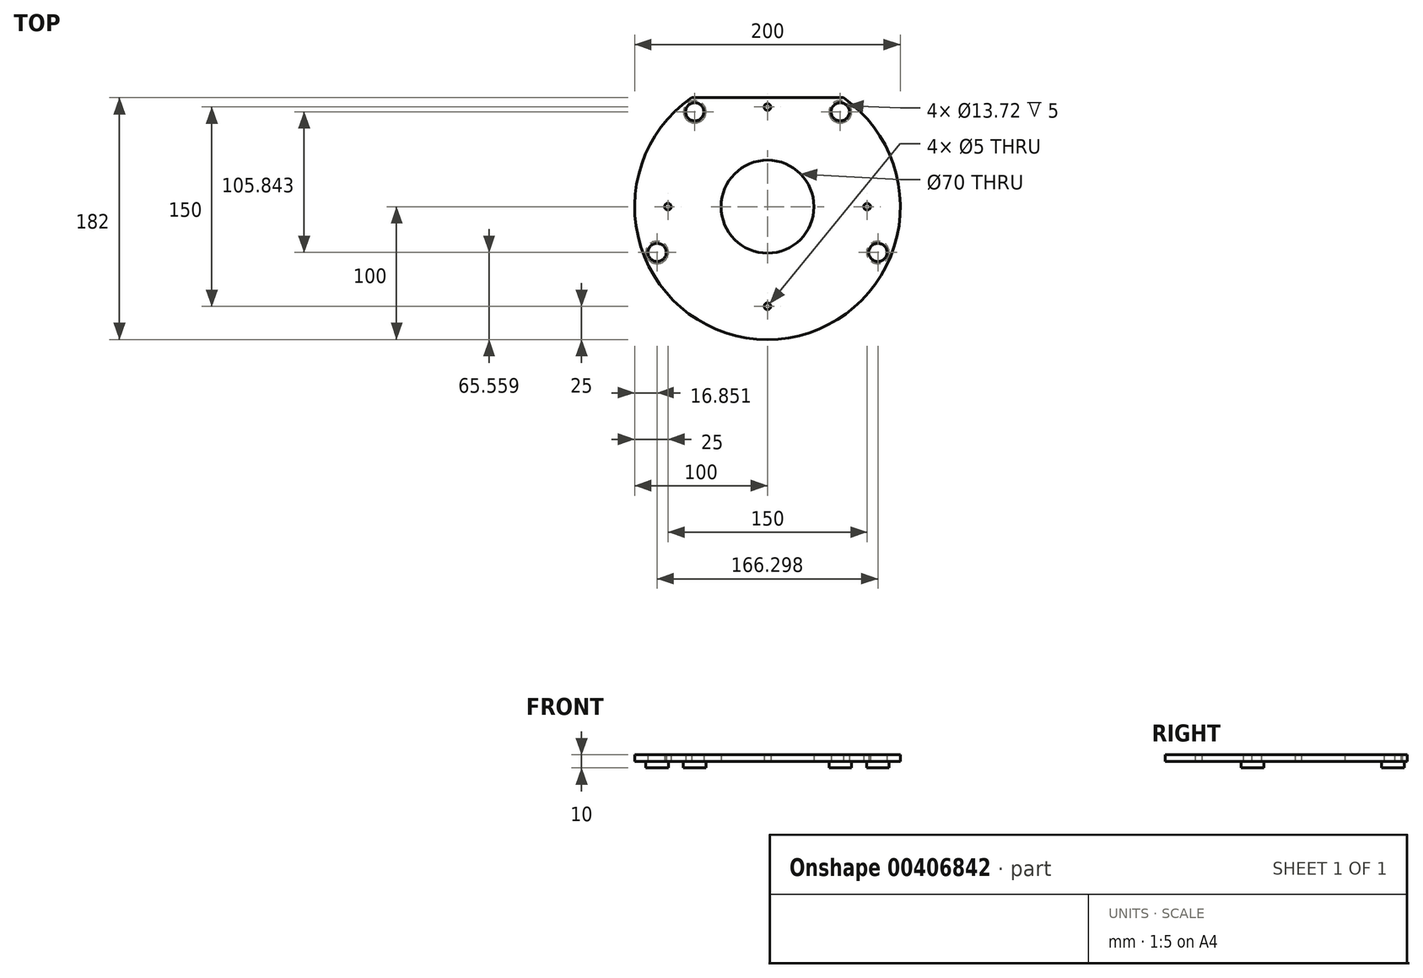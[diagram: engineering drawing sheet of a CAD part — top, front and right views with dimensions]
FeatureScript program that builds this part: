
annotation { "Feature Type Name" : "Feature", "Feature Type Description" : "" }
export const myFeature = defineFeature(function(context is Context, id is Id, definition is map)
    precondition{}
    {
        {
            var Q0;
            Q0=qCreatedBy(makeId("Top.planeOp"),FACE);
            var sketch = newSketch(context, id + "F0", { "sketchPlane" : qUnion([Q0])});
            skArc(sketch, "E0", {"start": v(-57.24, 82) * mm, "mid": v(0, -100) * mm, "end": v(57.24, 82) * mm});
            skCircle(sketch, "E1", {"center": v(-83.15, -34.44) * mm, "radius": 6.86 * mm});
            skLineSegment(sketch, "E2", {"start": v(-83.15, -34.44) * mm, "end": v(0, 0) * mm, "construction": true});
            skCircle(sketch, "E3.1.0", {"center": v(-54.79, 71.4) * mm, "radius": 6.86 * mm});
            skCircle(sketch, "E3.2.0", {"center": v(54.79, 71.4) * mm, "radius": 6.86 * mm});
            skCircle(sketch, "E3.3.0", {"center": v(83.15, -34.44) * mm, "radius": 6.86 * mm});
            skLineSegment(sketch, "E3.anchor1", {"start": v(0, 0) * mm, "end": v(-83.15, -34.44) * mm, "construction": true});
            skLineSegment(sketch, "E3.anchor2", {"start": v(0, 0) * mm, "end": v(83.15, -34.44) * mm, "construction": true});
            skLineSegment(sketch, "E4", {"start": v(-57.24, 82) * mm, "end": v(57.24, 82) * mm});
            skCircle(sketch, "E5", {"center": v(0, 0) * mm, "radius": 35 * mm});
            skCircle(sketch, "E6", {"center": v(-75, 0) * mm, "radius": 2.5 * mm});
            skCircle(sketch, "E7.1.0", {"center": v(0, -75) * mm, "radius": 2.5 * mm});
            skCircle(sketch, "E7.2.0", {"center": v(75, 0) * mm, "radius": 2.5 * mm});
            skCircle(sketch, "E7.3.0", {"center": v(0, 75) * mm, "radius": 2.5 * mm});
            skSolve(sketch);
        }
        {
            var Q0;
            Q0 = qSketchRegion(id + "F0", true);
            extrude(context, id + "F1", {"entities" : qUnion([Q0]), "depth" : 5 * mm});
        }
        {
            var Q0;
            Q0=makeQuery(id+"F1.opExtrude","CAP_FACE",FACE,{"disambiguationData":[OSD([sQuery(id+"F0.wireOp",EDGE,"E0"),sQuery(id+"F0.wireOp",EDGE,"E1"),sQuery(id+"F0.wireOp",EDGE,"E3.1.0"),sQuery(id+"F0.wireOp",EDGE,"E3.2.0"),sQuery(id+"F0.wireOp",EDGE,"E3.3.0"),sQuery(id+"F0.wireOp",EDGE,"E4"),sQuery(id+"F0.wireOp",EDGE,"E5"),sQuery(id+"F0.wireOp",EDGE,"E6"),sQuery(id+"F0.wireOp",EDGE,"E7.1.0"),sQuery(id+"F0.wireOp",EDGE,"E7.2.0"),sQuery(id+"F0.wireOp",EDGE,"E7.3.0")])],"isStart":true});
            var sketch = newSketch(context, id + "F2", { "sketchPlane" : qUnion([Q0])});
            skCircle(sketch, "E8", {"center": v(83.15, 34.44) * mm, "radius": 8.5 * mm});
            skCircle(sketch, "E9.1.0", {"center": v(54.79, -71.4) * mm, "radius": 8.5 * mm});
            skCircle(sketch, "E9.2.0", {"center": v(-54.79, -71.4) * mm, "radius": 8.5 * mm});
            skCircle(sketch, "E9.3.0", {"center": v(-83.15, 34.44) * mm, "radius": 8.5 * mm});
            skPoint(sketch, "E9.center", {"position": v(0, 0) * mm});
            skLineSegment(sketch, "E9.anchor1", {"start": v(0, 0) * mm, "end": v(83.15, 34.44) * mm, "construction": true});
            skLineSegment(sketch, "E9.anchor2", {"start": v(0, 0) * mm, "end": v(-83.15, 34.44) * mm, "construction": true});
            skSolve(sketch);
        }
        {
            var Q0;
            Q0 = qSketchRegion(id + "F2", true);
            extrude(context, id + "F3", {"entities" : qUnion([Q0]), "operationType" : NewBodyOperationType.ADD, "depth" : 5 * mm});
        }
    });
